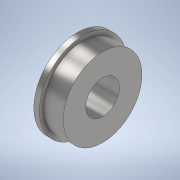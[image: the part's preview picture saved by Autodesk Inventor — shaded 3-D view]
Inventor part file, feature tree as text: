
AUTODESK INVENTOR PART (.ipt)
format: ipt  version: 2020 (Build 240168000, 168)  size: 139,776 bytes
history: native  units: in
note: dims shown in document units (in); Inventor stores cm internally (conversion verified against a paired STEP export)
features: revolve x1
ambient origin geometry x8: Origin, YZ Plane, XZ Plane, XY Plane, X Axis, Y Axis, Z Axis, Center Point
bodies: Solid1 (feature_tree)
feature tree (1):
  revolve  "Revolve1"  [1 undecoded]
note: 1 required parameter value undecoded (feature->parameter linkage not recoverable at this tier; creation-order binding heuristic only, values carry confidence <= 0.55)
